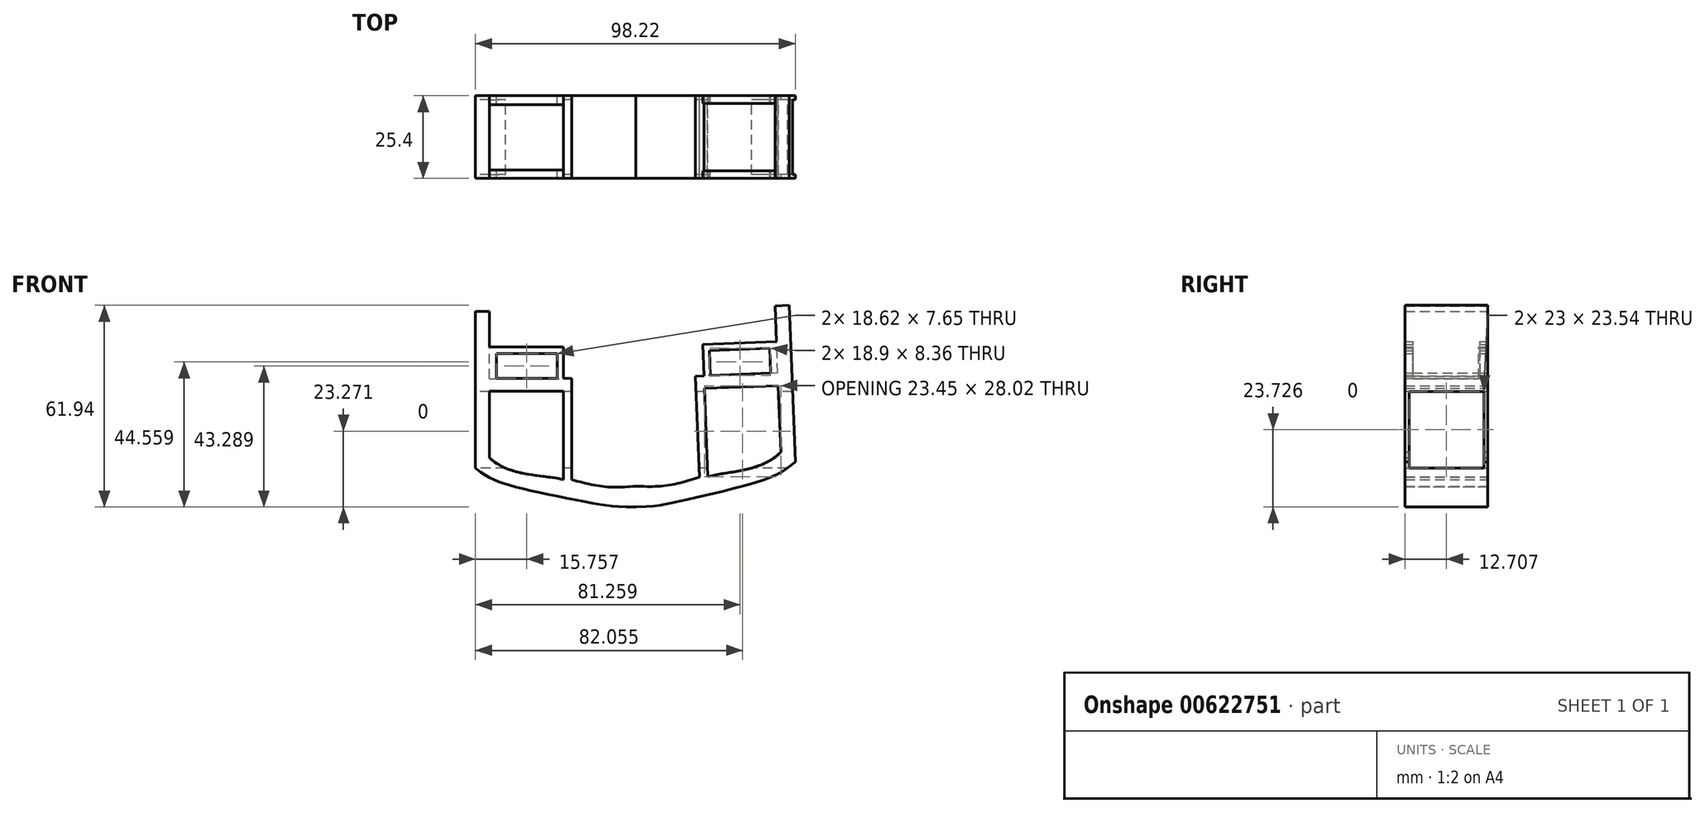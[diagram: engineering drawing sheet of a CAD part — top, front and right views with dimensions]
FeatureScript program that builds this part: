
annotation { "Feature Type Name" : "Feature", "Feature Type Description" : "" }
export const myFeature = defineFeature(function(context is Context, id is Id, definition is map)
    precondition{}
    {
        {
            var Q0;
            Q0=qCreatedBy(makeId("Front.planeOp"),FACE);
            var sketch = newSketch(context, id + "F0", { "sketchPlane" : qUnion([Q0])});
            skLineSegment(sketch, "E0", {"start": v(-92.33, 44.94) * mm, "end": v(-92.33, -3.17) * mm});
            skLineSegment(sketch, "E1", {"start": v(-92.33, 44.94) * mm, "end": v(-88.01, 44.94) * mm});
            skLineSegment(sketch, "E2", {"start": v(-88.01, 44.94) * mm, "end": v(-88.01, 34) * mm});
            skLineSegment(sketch, "E3", {"start": v(-88.01, 34) * mm, "end": v(-65.33, 34) * mm});
            skLineSegment(sketch, "E4", {"start": v(-65.33, 34) * mm, "end": v(-65.33, 24.34) * mm});
            skLineSegment(sketch, "E5", {"start": v(-65.33, 24.34) * mm, "end": v(-62.75, 24.34) * mm});
            skLineSegment(sketch, "E6", {"start": v(-62.75, 24.34) * mm, "end": v(-62.75, -6.73) * mm});
            skLineSegment(sketch, "E7", {"start": v(-62.75, -6.73) * mm, "end": v(-65.33, -6.73) * mm});
            skLineSegment(sketch, "E8", {"start": v(-65.33, -6.73) * mm, "end": v(-65.33, 20.43) * mm});
            skLineSegment(sketch, "E9", {"start": v(-65.33, 20.43) * mm, "end": v(-88.01, 20.43) * mm});
            skLineSegment(sketch, "E10", {"start": v(-88.01, 20.43) * mm, "end": v(-88.01, 24.34) * mm});
            skLineSegment(sketch, "E11", {"start": v(-88.01, 24.34) * mm, "end": v(-88.01, 34) * mm});
            skLineSegment(sketch, "E12", {"start": v(-85.88, 31.98) * mm, "end": v(-67.26, 31.98) * mm});
            skLineSegment(sketch, "E13", {"start": v(-67.26, 31.98) * mm, "end": v(-67.26, 24.34) * mm});
            skLineSegment(sketch, "E14", {"start": v(-67.26, 24.34) * mm, "end": v(-85.88, 24.34) * mm});
            skLineSegment(sketch, "E15", {"start": v(-85.88, 24.34) * mm, "end": v(-85.88, 31.98) * mm});
            skLineSegment(sketch, "E16", {"start": v(-88.01, 20.43) * mm, "end": v(-88.01, 0) * mm});
            skFitSpline(sketch, "E17", {"points": [v(-88.01, 0) * mm, v(-84.47, -2.53) * mm, v(-76.62, -5.01) * mm, v(-65.33, -6.73) * mm], "startDerivative": vector(11.24, -10.59) * mm, "endDerivative": vector(23.68, -5.89) * mm});
            skFitSpline(sketch, "E18", {"points": [v(-92.33, -3.17) * mm, v(-87.16, -6.55) * mm, v(-81.51, -8.55) * mm, v(-68.25, -11.65) * mm, v(-53.68, -14.39) * mm, v(-42.97, -15.11) * mm, v(15.57, -9.33) * mm], "startDerivative": vector(61.35, -47.21) * mm, "endDerivative": vector(118.27, 30.88) * mm});
            skLineSegment(sketch, "E19", {"start": v(-44.26, 51.63) * mm, "end": v(-42.97, -15.11) * mm});
            skLineSegment(sketch, "E20.MirrorCS", {"start": v(-22.15, 25.17) * mm, "end": v(-24.73, 25.07) * mm});
            skLineSegment(sketch, "E21.MirrorCS", {"start": v(-23.52, -5.97) * mm, "end": v(-20.95, -5.87) * mm});
            skLineSegment(sketch, "E22.MirrorCS", {"start": v(0.66, 22.15) * mm, "end": v(0.5, 26.05) * mm});
            skLineSegment(sketch, "E23.MirrorCS", {"start": v(-20.52, 32.89) * mm, "end": v(-20.22, 25.25) * mm});
            skFitSpline(sketch, "E24.MirrorCS", {"points": [v(1.45, 1.74) * mm, v(-1.99, -0.93) * mm, v(-9.73, -3.72) * mm, v(-20.95, -5.87) * mm], "startDerivative": vector(-10.82, -11.02) * mm, "endDerivative": vector(-23.44, -6.8) * mm});
            skLineSegment(sketch, "E25.MirrorCS", {"start": v(-24.73, 25.07) * mm, "end": v(-23.52, -5.97) * mm});
            skLineSegment(sketch, "E26.MirrorCS", {"start": v(0.13, 35.72) * mm, "end": v(-22.53, 34.84) * mm});
            skLineSegment(sketch, "E27.MirrorCS", {"start": v(0.66, 22.15) * mm, "end": v(1.45, 1.74) * mm});
            skLineSegment(sketch, "E28.MirrorCS", {"start": v(-1.62, 25.97) * mm, "end": v(-1.91, 33.61) * mm});
            skLineSegment(sketch, "E29.MirrorCS", {"start": v(-22.53, 34.84) * mm, "end": v(-22.15, 25.17) * mm});
            skLineSegment(sketch, "E30.MirrorCS", {"start": v(-20.95, -5.87) * mm, "end": v(-22, 21.27) * mm});
            skLineSegment(sketch, "E31.MirrorCS", {"start": v(-1.91, 33.61) * mm, "end": v(-20.52, 32.89) * mm});
            skLineSegment(sketch, "E32.MirrorCS", {"start": v(-22, 21.27) * mm, "end": v(0.66, 22.15) * mm});
            skLineSegment(sketch, "E33.MirrorCS", {"start": v(4.03, 46.8) * mm, "end": v(5.9, -1.27) * mm});
            skLineSegment(sketch, "E34.MirrorCS", {"start": v(4.03, 46.8) * mm, "end": v(-0.3, 46.64) * mm});
            skLineSegment(sketch, "E35.MirrorCS", {"start": v(-20.22, 25.25) * mm, "end": v(-1.62, 25.97) * mm});
            skLineSegment(sketch, "E36.MirrorCS", {"start": v(-0.3, 46.64) * mm, "end": v(0.13, 35.72) * mm});
            skLineSegment(sketch, "E37.MirrorCS", {"start": v(0.5, 26.05) * mm, "end": v(0.13, 35.72) * mm});
            skFitSpline(sketch, "E38.MirrorCS", {"points": [v(5.9, -1.27) * mm, v(0.86, -4.85) * mm, v(-4.71, -7.06) * mm, v(-17.84, -10.67) * mm, v(-32.3, -13.97) * mm, v(-42.97, -15.11) * mm, v(-101.69, -11.6) * mm], "startDerivative": vector(-59.47, -49.56) * mm, "endDerivative": vector(-119.38, 26.27) * mm});
            skFitSpline(sketch, "E39", {"points": [v(-62.75, -6.73) * mm, v(-52.83, -8.88) * mm, v(-43.1, -8.77) * mm], "startDerivative": vector(19.63, -5.38) * mm, "endDerivative": vector(19.7, 1.32) * mm});
            skFitSpline(sketch, "E40.MirrorCS", {"points": [v(-23.52, -5.97) * mm, v(-33.36, -8.5) * mm, v(-43.1, -8.77) * mm], "startDerivative": vector(-19.4, -6.13) * mm, "endDerivative": vector(-19.73, 0.56) * mm});
            skSolve(sketch);
        }
        {
            var Q0;
            Q0=makeQuery(id+"F0.imprint","IMPRINT",FACE,{"disambiguationData":[TD([[makeQuery(id+"F0.imprint","IMPRINT",EDGE,{"derivedFrom":sQuery(id+"F0.wireOp",EDGE,"E0")}),1.0]])]});
            var Q1;
            Q1=makeQuery(id+"F0.imprint","IMPRINT",FACE,{"disambiguationData":[TD([[makeQuery(id+"F0.imprint","IMPRINT",EDGE,{"derivedFrom":sQuery(id+"F0.wireOp",EDGE,"E21.MirrorCS")}),-1.0]])]});
            var Q2;
            Q2=makeQuery(id+"F0.imprint","IMPRINT",FACE,{"disambiguationData":[TD([[makeQuery(id+"F0.imprint","IMPRINT",EDGE,{"derivedFrom":sQuery(id+"F0.wireOp",EDGE,"E20.MirrorCS")}),1.0]])]});
            var Q3;
            Q3=makeQuery(id+"F0.imprint","IMPRINT",FACE,{"disambiguationData":[TD([[makeQuery(id+"F0.imprint","IMPRINT",EDGE,{"derivedFrom":sQuery(id+"F0.wireOp",EDGE,"E3")}),-1.0]])]});
            extrude(context, id + "F1", {"entities" : qUnion([Q0, Q1, Q2, Q3]), "depth" : 25.4 * mm, "offsetDistance" : 25.4 * mm});
        }
        {
            var Q0;
            Q0=makeQuery(id+"F1.opExtrude","SWEPT_FACE",FACE,{"disambiguationData":[OSD([sQuery(id+"F0.wireOp",EDGE,"E0")])]});
            var sketch = newSketch(context, id + "F2", { "sketchPlane" : qUnion([Q0])});
            skLineSegment(sketch, "E41.bottom", {"start": v(1.2, 20.37) * mm, "end": v(24.2, 20.37) * mm});
            skLineSegment(sketch, "E41.top", {"start": v(1.2, -3.17) * mm, "end": v(24.2, -3.17) * mm});
            skLineSegment(sketch, "E41.left", {"start": v(1.2, 20.37) * mm, "end": v(1.2, -3.17) * mm});
            skLineSegment(sketch, "E41.right", {"start": v(24.2, 20.37) * mm, "end": v(24.2, -3.17) * mm});
            skSolve(sketch);
        }
        {
            var Q0;
            Q0=makeQuery(id+"F2.imprint","IMPRINT",FACE,{"disambiguationData":[TD([[makeQuery(id+"F2.imprint","IMPRINT",EDGE,{"derivedFrom":sQuery(id+"F2.wireOp",EDGE,"E41.bottom")}),-1.0]])]});
            extrude(context, id + "F3", {"entities" : qUnion([Q0]), "operationType" : NewBodyOperationType.REMOVE, "oppositeDirection" : true, "depth" : 200 * mm, "offsetDistance" : 25 * mm});
        }
        {
            var Q0;
            Q0=makeQuery(id+"F1.opExtrude","SWEPT_FACE",FACE,{"disambiguationData":[OSD([sQuery(id+"F0.wireOp",EDGE,"E3")])]});
            var sketch = newSketch(context, id + "F4", { "sketchPlane" : qUnion([Q0])});
            skLineSegment(sketch, "E42.bottom", {"start": v(-88.01, -22.83) * mm, "end": v(-65.33, -22.83) * mm});
            skLineSegment(sketch, "E42.top", {"start": v(-88.01, -2.76) * mm, "end": v(-65.33, -2.76) * mm});
            skLineSegment(sketch, "E42.left", {"start": v(-88.01, -22.83) * mm, "end": v(-88.01, -2.76) * mm});
            skLineSegment(sketch, "E42.right", {"start": v(-65.33, -22.83) * mm, "end": v(-65.33, -2.76) * mm});
            skSolve(sketch);
        }
        {
            var Q0;
            Q0=makeQuery(id+"F4.imprint","IMPRINT",FACE,{"disambiguationData":[TD([[makeQuery(id+"F4.imprint","IMPRINT",EDGE,{"derivedFrom":sQuery(id+"F4.wireOp",EDGE,"E42.bottom")}),1.0]])]});
            extrude(context, id + "F5", {"entities" : qUnion([Q0]), "operationType" : NewBodyOperationType.REMOVE, "oppositeDirection" : true, "depth" : 9.7 * mm, "offsetDistance" : 25 * mm});
        }
        {
            var Q0;
            Q0=makeQuery(id+"F1.opExtrude","SWEPT_FACE",FACE,{"disambiguationData":[OSD([sQuery(id+"F0.wireOp",EDGE,"E26.MirrorCS")])]});
            var sketch = newSketch(context, id + "F6", { "sketchPlane" : qUnion([Q0])});
            skLineSegment(sketch, "E43.bottom", {"start": v(1.52, -2.4) * mm, "end": v(-21.16, -2.4) * mm});
            skLineSegment(sketch, "E43.top", {"start": v(1.52, -23.05) * mm, "end": v(-21.16, -23.05) * mm});
            skLineSegment(sketch, "E43.left", {"start": v(1.52, -2.4) * mm, "end": v(1.52, -23.05) * mm});
            skLineSegment(sketch, "E43.right", {"start": v(-21.16, -2.4) * mm, "end": v(-21.16, -23.05) * mm});
            skSolve(sketch);
        }
        {
            var Q0;
            Q0=makeQuery(id+"F6.imprint","IMPRINT",FACE,{"disambiguationData":[TD([[makeQuery(id+"F6.imprint","IMPRINT",EDGE,{"derivedFrom":sQuery(id+"F6.wireOp",EDGE,"E43.bottom")}),1.0]])]});
            extrude(context, id + "F7", {"entities" : qUnion([Q0]), "operationType" : NewBodyOperationType.REMOVE, "oppositeDirection" : true, "depth" : 9.7 * mm, "offsetDistance" : 25 * mm});
        }
    });
